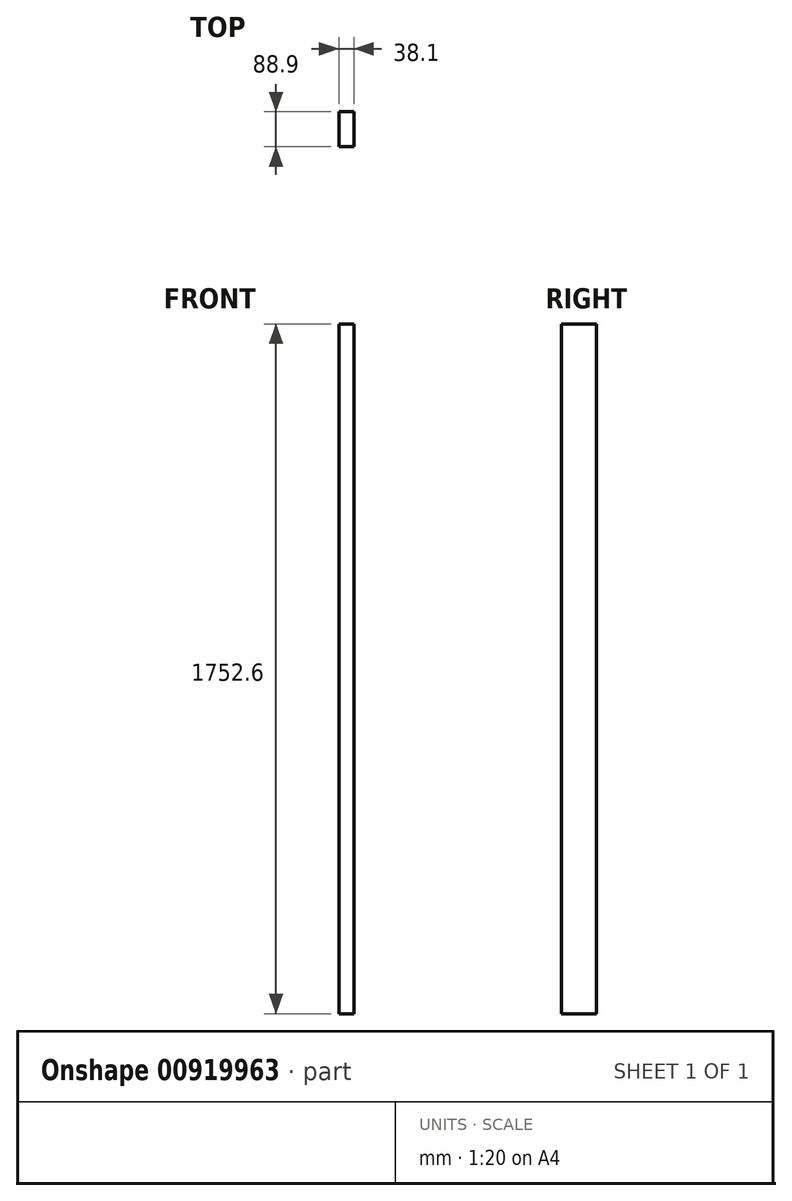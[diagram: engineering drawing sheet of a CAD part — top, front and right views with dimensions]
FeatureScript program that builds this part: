
annotation { "Feature Type Name" : "Feature", "Feature Type Description" : "" }
export const myFeature = defineFeature(function(context is Context, id is Id, definition is map)
    precondition{}
    {
        {
            var Q0;
            Q0=qCreatedBy(makeId("Top.planeOp"),FACE);
            var sketch = newSketch(context, id + "F0", { "sketchPlane" : qUnion([Q0])});
            skLineSegment(sketch, "E0.bottom", {"start": v(-19.05, 44.45) * mm, "end": v(19.05, 44.45) * mm});
            skLineSegment(sketch, "E0.top", {"start": v(-19.05, -44.45) * mm, "end": v(19.05, -44.45) * mm});
            skLineSegment(sketch, "E0.left", {"start": v(-19.05, 44.45) * mm, "end": v(-19.05, -44.45) * mm});
            skLineSegment(sketch, "E0.right", {"start": v(19.05, 44.45) * mm, "end": v(19.05, -44.45) * mm});
            skPoint(sketch, "E1", {"position": v(0, 44.45) * mm});
            skPoint(sketch, "E2", {"position": v(19.05, 0) * mm});
            skSolve(sketch);
        }
        {
            var Q0;
            Q0=qSketchRegion(id+"F0",true);
            extrude(context, id + "F1", {"entities" : qUnion([Q0]), "depth" : 1752.6 * mm, "offsetDistance" : 25 * mm});
        }
    });
